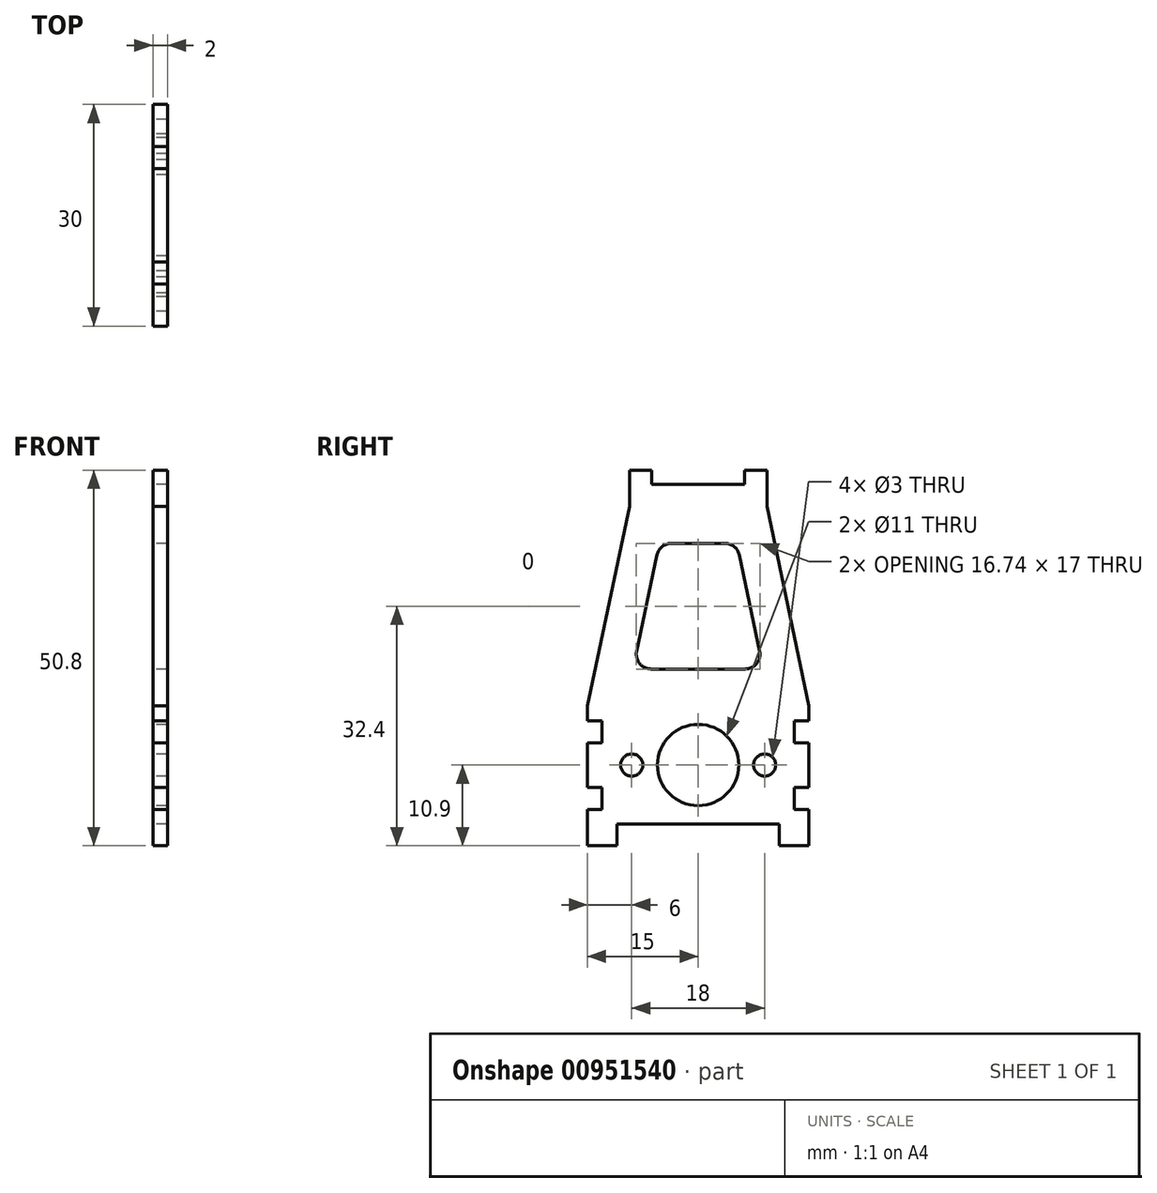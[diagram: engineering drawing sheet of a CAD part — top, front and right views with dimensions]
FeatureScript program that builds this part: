
annotation { "Feature Type Name" : "Feature", "Feature Type Description" : "" }
export const myFeature = defineFeature(function(context is Context, id is Id, definition is map)
    precondition{}
    {
        {
            var Q0;
            Q0=qCreatedBy(makeId("Right.planeOp"),FACE);
            var sketch = newSketch(context, id + "F0", { "sketchPlane" : qUnion([Q0])});
            skLineSegment(sketch, "E0.bottom", {"start": v(-15, -8) * mm, "end": v(15, -8) * mm});
            skLineSegment(sketch, "E0.top", {"start": v(-15, 8) * mm, "end": v(15, 8) * mm});
            skLineSegment(sketch, "E0.left", {"start": v(-15, -8) * mm, "end": v(-15, 8) * mm});
            skLineSegment(sketch, "E0.right", {"start": v(15, -8) * mm, "end": v(15, 8) * mm});
            skPoint(sketch, "E0.middle", {"position": v(0, 0) * mm});
            skLineSegment(sketch, "E1.bottom", {"start": v(-9.3, 35) * mm, "end": v(9.3, 35) * mm});
            skLineSegment(sketch, "E1.top", {"start": v(-9.3, 38) * mm, "end": v(9.3, 38) * mm});
            skLineSegment(sketch, "E1.left", {"start": v(-9.3, 35) * mm, "end": v(-9.3, 38) * mm});
            skLineSegment(sketch, "E1.right", {"start": v(9.3, 35) * mm, "end": v(9.3, 38) * mm});
            skPoint(sketch, "E1.middle", {"position": v(0, 36.5) * mm});
            skCircle(sketch, "E2", {"center": v(0, 0) * mm, "radius": 5.5 * mm});
            skLineSegment(sketch, "E3", {"start": v(-9.3, 35) * mm, "end": v(-15, 8) * mm});
            skLineSegment(sketch, "E4", {"start": v(9.3, 35) * mm, "end": v(15, 8) * mm});
            skLineSegment(sketch, "E5", {"start": v(9.3, 38) * mm, "end": v(9.3, 39.9) * mm});
            skLineSegment(sketch, "E6", {"start": v(9.3, 39.9) * mm, "end": v(6.3, 39.9) * mm});
            skLineSegment(sketch, "E7", {"start": v(6.3, 39.9) * mm, "end": v(6.3, 38) * mm});
            skLineSegment(sketch, "E8", {"start": v(-9.3, 38) * mm, "end": v(-9.3, 39.9) * mm});
            skLineSegment(sketch, "E9", {"start": v(-9.3, 39.9) * mm, "end": v(-6.3, 39.9) * mm});
            skLineSegment(sketch, "E10", {"start": v(-6.3, 39.9) * mm, "end": v(-6.3, 38) * mm});
            skLineSegment(sketch, "E11", {"start": v(15, -8) * mm, "end": v(15, -10.9) * mm});
            skLineSegment(sketch, "E12", {"start": v(15, -10.9) * mm, "end": v(11, -10.9) * mm});
            skLineSegment(sketch, "E13", {"start": v(11, -10.9) * mm, "end": v(11, -8) * mm});
            skLineSegment(sketch, "E14", {"start": v(-15, -8) * mm, "end": v(-15, -10.9) * mm});
            skLineSegment(sketch, "E15", {"start": v(-15, -10.9) * mm, "end": v(-11, -10.9) * mm});
            skLineSegment(sketch, "E16", {"start": v(-11, -10.9) * mm, "end": v(-11, -8) * mm});
            skLineSegment(sketch, "E17.0", {"start": v(5.58, 28.41) * mm, "end": v(8.33, 15.41) * mm});
            skLineSegment(sketch, "E17.1", {"start": v(-3.63, 30) * mm, "end": v(3.63, 30) * mm});
            skLineSegment(sketch, "E17.2", {"start": v(-5.58, 28.41) * mm, "end": v(-8.33, 15.41) * mm});
            skLineSegment(sketch, "E17.3", {"start": v(-6.37, 13) * mm, "end": v(6.37, 13) * mm});
            skPoint(sketch, "E18.visualSharp", {"position": v(5.25, 30) * mm});
            skArc(sketch, "E18.filletArc", {"start": v(5.58, 28.41) * mm, "mid": v(4.89, 29.55) * mm, "end": v(3.63, 30) * mm});
            skPoint(sketch, "E19.visualSharp", {"position": v(-5.25, 30) * mm});
            skArc(sketch, "E19.filletArc", {"start": v(-3.63, 30) * mm, "mid": v(-4.89, 29.55) * mm, "end": v(-5.58, 28.41) * mm});
            skPoint(sketch, "E20.visualSharp", {"position": v(-8.84, 13) * mm});
            skArc(sketch, "E20.filletArc", {"start": v(-8.33, 15.41) * mm, "mid": v(-7.92, 13.74) * mm, "end": v(-6.37, 13) * mm});
            skPoint(sketch, "E21.visualSharp", {"position": v(8.84, 13) * mm});
            skArc(sketch, "E21.filletArc", {"start": v(6.37, 13) * mm, "mid": v(7.92, 13.74) * mm, "end": v(8.33, 15.41) * mm});
            skLineSegment(sketch, "E22", {"start": v(15, 6) * mm, "end": v(13, 6) * mm});
            skLineSegment(sketch, "E23", {"start": v(13, 6) * mm, "end": v(13, 3) * mm});
            skLineSegment(sketch, "E24", {"start": v(13, 3) * mm, "end": v(15, 3) * mm});
            skLineSegment(sketch, "E25", {"start": v(15, -3) * mm, "end": v(13, -3) * mm});
            skLineSegment(sketch, "E26", {"start": v(13, -3) * mm, "end": v(13, -6) * mm});
            skLineSegment(sketch, "E27", {"start": v(13, -6) * mm, "end": v(15, -6) * mm});
            skLineSegment(sketch, "E28", {"start": v(-15, 6) * mm, "end": v(-13, 6) * mm});
            skLineSegment(sketch, "E29", {"start": v(-13, 6) * mm, "end": v(-13, 3) * mm});
            skLineSegment(sketch, "E30", {"start": v(-13, 3) * mm, "end": v(-15, 3) * mm});
            skLineSegment(sketch, "E31", {"start": v(-15, -3) * mm, "end": v(-13, -3) * mm});
            skLineSegment(sketch, "E32", {"start": v(-13, -3) * mm, "end": v(-13, -6) * mm});
            skLineSegment(sketch, "E33", {"start": v(-13, -6) * mm, "end": v(-15, -6) * mm});
            skCircle(sketch, "E34", {"center": v(-9, 0) * mm, "radius": 1.5 * mm});
            skCircle(sketch, "E35", {"center": v(9, 0) * mm, "radius": 1.5 * mm});
            skSolve(sketch);
        }
        {
            var Q0;
            {var subQ0=sQuery(id+"F0.wireOp",EDGE,"E14");Q0=makeQuery(id+"F0.imprint","IMPRINT",FACE,{"disambiguationData":[TD([[makeQuery(id+"F0.imprint","IMPRINT",EDGE,{"derivedFrom":subQ0}),1.0]])]});}
            var Q1;
            {var subQ0=sQuery(id+"F0.wireOp",EDGE,"E11");Q1=makeQuery(id+"F0.imprint","IMPRINT",FACE,{"disambiguationData":[TD([[makeQuery(id+"F0.imprint","IMPRINT",EDGE,{"derivedFrom":subQ0}),-1.0]])]});}
            var Q2;
            {var subQ0=sQuery(id+"F0.wireOp",EDGE,"E8");Q2=makeQuery(id+"F0.imprint","IMPRINT",FACE,{"disambiguationData":[TD([[makeQuery(id+"F0.imprint","IMPRINT",EDGE,{"derivedFrom":subQ0}),-1.0]])]});}
            var Q3;
            {var subQ0=sQuery(id+"F0.wireOp",EDGE,"E5");Q3=makeQuery(id+"F0.imprint","IMPRINT",FACE,{"disambiguationData":[TD([[makeQuery(id+"F0.imprint","IMPRINT",EDGE,{"derivedFrom":subQ0}),1.0]])]});}
            var Q4;
            Q4=makeQuery(id+"F0.imprint","IMPRINT",FACE,{"disambiguationData":[TD([[makeQuery(id+"F0.imprint","IMPRINT",EDGE,{"derivedFrom":sQuery(id+"F0.wireOp",EDGE,"E1.bottom")}),1.0]])]});
            var Q5;
            {var subQ12=sQuery(id+"F0.wireOp",EDGE,"E0.top");Q5=makeQuery(id+"F0.imprint","IMPRINT",FACE,{"disambiguationData":[TD([[makeQuery(id+"F0.imprint","IMPRINT",EDGE,{"derivedFrom":subQ12}),-1.0]])]});}
            var Q6;
            Q6=makeQuery(id+"F0.imprint","IMPRINT",FACE,{"disambiguationData":[TD([[makeQuery(id+"F0.imprint","IMPRINT",EDGE,{"derivedFrom":sQuery(id+"F0.wireOp",EDGE,"E0.top")}),1.0]])]});
            extrude(context, id + "F1", {"entities" : qUnion([Q0, Q1, Q2, Q3, Q4, Q5, Q6]), "depth" : 2 * mm, "offsetDistance" : 25 * mm});
        }
        {
            var Q0;
            Q0=makeQuery(id+"F0.imprint","IMPRINT",FACE,{"disambiguationData":[TD([[makeQuery(id+"F0.imprint","IMPRINT",EDGE,{"derivedFrom":sQuery(id+"F0.wireOp",EDGE,"E0.top")}),1.0]])]});
            var Q1;
            Q1=makeQuery(id+"F0.imprint","IMPRINT",FACE,{"disambiguationData":[TD([[makeQuery(id+"F0.imprint","IMPRINT",EDGE,{"derivedFrom":sQuery(id+"F0.wireOp",EDGE,"E0.top")}),-1.0]])]});
            var Q2;
            {var subQ0=sQuery(id+"F0.wireOp",EDGE,"E14");Q2=makeQuery(id+"F0.imprint","IMPRINT",FACE,{"disambiguationData":[TD([[makeQuery(id+"F0.imprint","IMPRINT",EDGE,{"derivedFrom":subQ0}),1.0]])]});}
            var Q3;
            {var subQ0=sQuery(id+"F0.wireOp",EDGE,"E11");Q3=makeQuery(id+"F0.imprint","IMPRINT",FACE,{"disambiguationData":[TD([[makeQuery(id+"F0.imprint","IMPRINT",EDGE,{"derivedFrom":subQ0}),-1.0]])]});}
            var Q4;
            {var subQ0=sQuery(id+"F0.wireOp",EDGE,"E5");Q4=makeQuery(id+"F0.imprint","IMPRINT",FACE,{"disambiguationData":[TD([[makeQuery(id+"F0.imprint","IMPRINT",EDGE,{"derivedFrom":subQ0}),1.0]])]});}
            var Q5;
            Q5=makeQuery(id+"F0.imprint","IMPRINT",FACE,{"disambiguationData":[TD([[makeQuery(id+"F0.imprint","IMPRINT",EDGE,{"derivedFrom":sQuery(id+"F0.wireOp",EDGE,"E1.bottom")}),1.0]])]});
            var Q6;
            {var subQ0=sQuery(id+"F0.wireOp",EDGE,"E8");Q6=makeQuery(id+"F0.imprint","IMPRINT",FACE,{"disambiguationData":[TD([[makeQuery(id+"F0.imprint","IMPRINT",EDGE,{"derivedFrom":subQ0}),-1.0]])]});}
            extrude(context, id + "F2", {"entities" : qUnion([Q0, Q1, Q2, Q3, Q4, Q5, Q6]), "depth" : 2 * mm, "offsetDistance" : 25 * mm});
        }
    });
